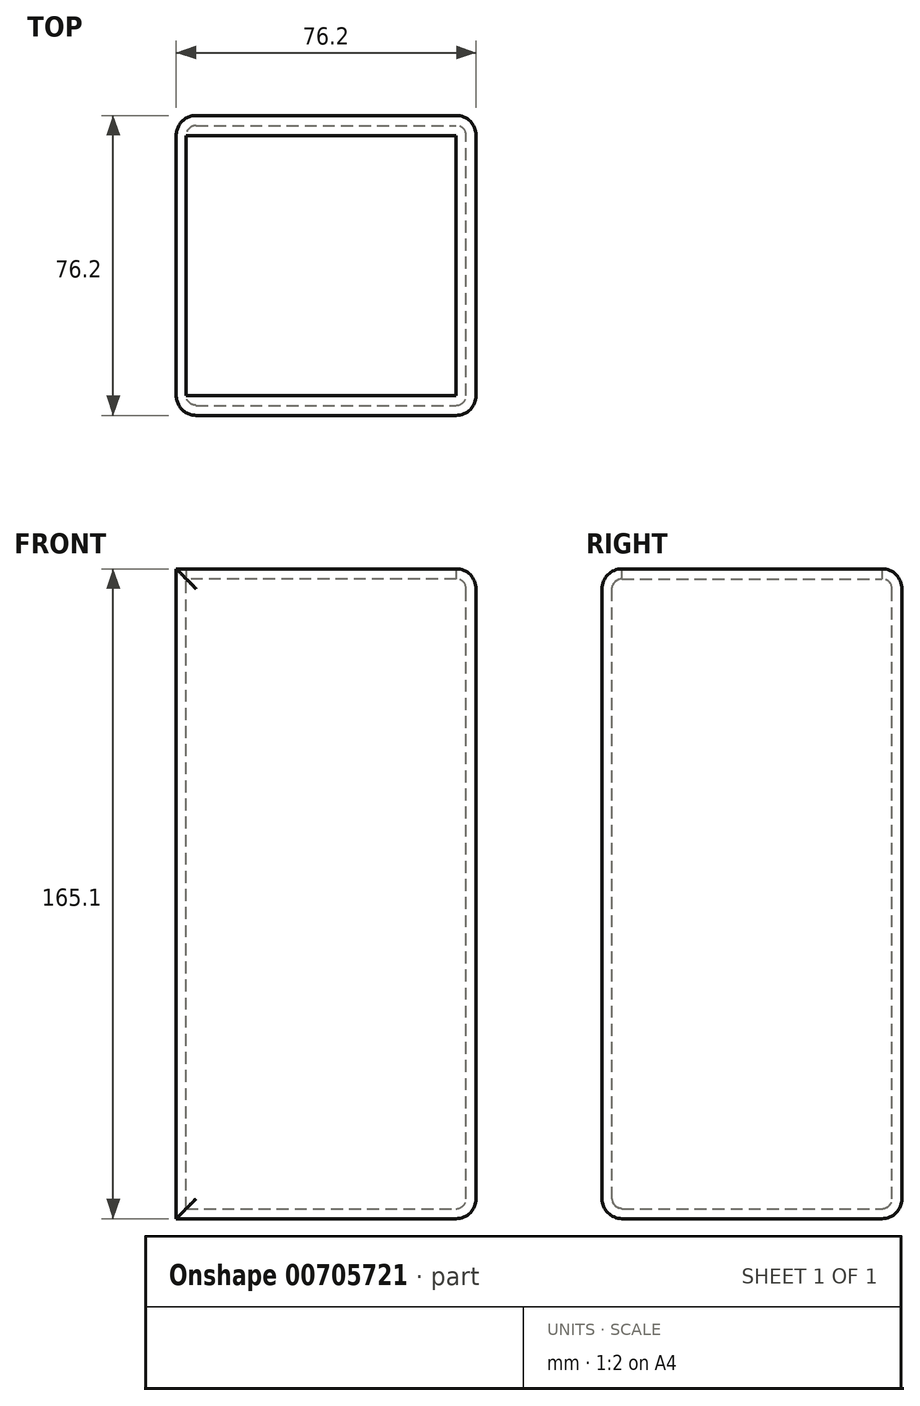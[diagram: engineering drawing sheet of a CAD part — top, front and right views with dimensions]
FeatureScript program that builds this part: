
annotation { "Feature Type Name" : "Feature", "Feature Type Description" : "" }
export const myFeature = defineFeature(function(context is Context, id is Id, definition is map)
    precondition{}
    {
        {
            var Q0;
            Q0=qCreatedBy(makeId("Right.planeOp"),FACE);
            var sketch = newSketch(context, id + "F0", { "sketchPlane" : qUnion([Q0])});
            skLineSegment(sketch, "E0.bottom", {"start": v(-38.1, 82.55) * mm, "end": v(38.1, 82.55) * mm});
            skLineSegment(sketch, "E0.top", {"start": v(-38.1, -82.55) * mm, "end": v(38.1, -82.55) * mm});
            skLineSegment(sketch, "E0.left", {"start": v(-38.1, 82.55) * mm, "end": v(-38.1, -82.55) * mm});
            skLineSegment(sketch, "E0.right", {"start": v(38.1, 82.55) * mm, "end": v(38.1, -82.55) * mm});
            skPoint(sketch, "E0.middle", {"position": v(0, 0) * mm});
            skSolve(sketch);
        }
        {
            var Q0;
            Q0=makeQuery(id+"F0.imprint","IMPRINT",FACE,{"disambiguationData":[TD([[makeQuery(id+"F0.imprint","IMPRINT",EDGE,{"derivedFrom":sQuery(id+"F0.wireOp",EDGE,"E0.bottom")}),-1.0]])]});
            extrude(context, id + "F1", {"entities" : qUnion([Q0]), "depth" : 76.2 * mm, "offsetDistance" : 25.4 * mm});
        }
        {
            var Q0;
            Q0=makeQuery(id+"F1.opExtrude","CAP_FACE",FACE,{"disambiguationData":[OSD([sQuery(id+"F0.wireOp",EDGE,"E0.bottom"),sQuery(id+"F0.wireOp",EDGE,"E0.top"),sQuery(id+"F0.wireOp",EDGE,"E0.left"),sQuery(id+"F0.wireOp",EDGE,"E0.right")])],"isStart":false});
            fillet(context, id + "F2", {"entities" : qUnion([Q0]), "radius" : 5.08 * mm, "tangentPropagation" : true, "allowEdgeOverflow" : false});
        }
        {
            var Q0;
            Q0=makeQuery(id+"F1.opExtrude","SWEPT_FACE",FACE,{"disambiguationData":[OSD([sQuery(id+"F0.wireOp",EDGE,"E0.right")])]});
            fillet(context, id + "F3", {"entities" : qUnion([Q0]), "radius" : 5.08 * mm, "tangentPropagation" : true, "allowEdgeOverflow" : false});
        }
        {
            var Q0;
            Q0=makeQuery(id+"F1.opExtrude","SWEPT_FACE",FACE,{"disambiguationData":[OSD([sQuery(id+"F0.wireOp",EDGE,"E0.left")])]});
            fillet(context, id + "F4", {"entities" : qUnion([Q0]), "radius" : 5.08 * mm, "tangentPropagation" : true, "allowEdgeOverflow" : false});
        }
        {
            var Q0;
            Q0=makeQuery(id+"F1.opExtrude","SWEPT_FACE",FACE,{"disambiguationData":[OSD([sQuery(id+"F0.wireOp",EDGE,"E0.bottom")])]});
            shell(context, id + "F5", {"entities" : qUnion([Q0]), "thickness" : 2.54 * mm});
        }
    });
